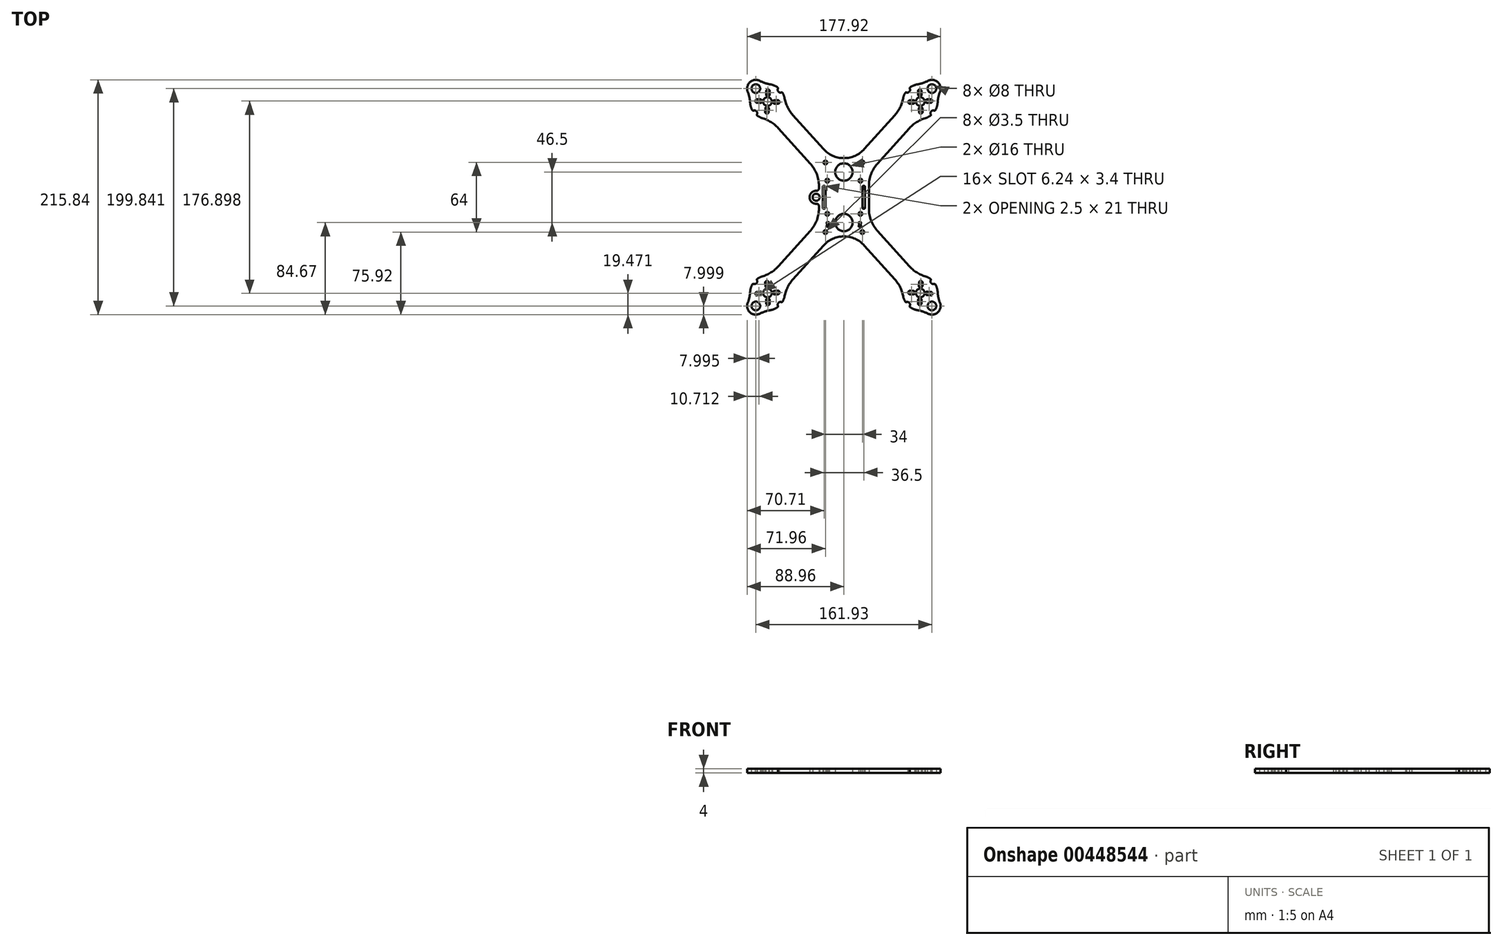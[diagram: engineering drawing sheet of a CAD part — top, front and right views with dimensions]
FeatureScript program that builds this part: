
annotation { "Feature Type Name" : "Feature", "Feature Type Description" : "" }
export const myFeature = defineFeature(function(context is Context, id is Id, definition is map)
    precondition{}
    {
        {
            var Q0;
            Q0=qCreatedBy(makeId("Top.planeOp"),FACE);
            var sketch = newSketch(context, id + "F0", { "sketchPlane" : qUnion([Q0])});
            skLineSegment(sketch, "E0", {"start": v(0, 10) * mm, "end": v(-70.26, 88.03) * mm, "construction": true});
            skCircle(sketch, "E1", {"center": v(-17, 32) * mm, "radius": 1.75 * mm});
            skCircle(sketch, "E2", {"center": v(-15.25, 15.25) * mm, "radius": 1.75 * mm});
            skLineSegment(sketch, "E3", {"start": v(-60.25, 63.46) * mm, "end": v(-30.82, 30.78) * mm});
            skLineSegment(sketch, "E4", {"start": v(-46.87, 75.5) * mm, "end": v(-18.86, 44.4) * mm});
            skLineSegment(sketch, "E5", {"start": v(-18.5, 10.5) * mm, "end": v(-18, 10.5) * mm});
            skArc(sketch, "E6", {"start": v(-54.54, 91) * mm, "mid": v(-55.24, 93.53) * mm, "end": v(-56.34, 95.93) * mm});
            skLineSegment(sketch, "E7.trimOffspring", {"start": v(-68.1, 72.18) * mm, "end": v(-68.1, 72.18) * mm});
            skCircle(sketch, "E8", {"center": v(-70.26, 88.03) * mm, "radius": 14 * mm, "construction": true});
            skCircle(sketch, "E9", {"center": v(-70.26, 88.03) * mm, "radius": 4 * mm});
            skArc(sketch, "E10", {"start": v(-30.5, 30.41) * mm, "mid": v(-30.66, 30.6) * mm, "end": v(-30.82, 30.78) * mm});
            skArc(sketch, "E11", {"start": v(-18.86, 44.4) * mm, "mid": v(-10.32, 38.2) * mm, "end": v(0, 36) * mm});
            skArc(sketch, "E12", {"start": v(0, 31.25) * mm, "mid": v(-8, 23.25) * mm, "end": v(0, 15.25) * mm});
            skPoint(sketch, "E13.visualSharp", {"position": v(-20.22, 10.5) * mm});
            skPoint(sketch, "E14.visualSharp", {"position": v(-54.72, 84.22) * mm});
            skArc(sketch, "E14.filletArc", {"start": v(-54.54, 91) * mm, "mid": v(-51.77, 82.72) * mm, "end": v(-46.87, 75.5) * mm});
            skPoint(sketch, "E15.visualSharp", {"position": v(-68.1, 72.18) * mm});
            skArc(sketch, "E15.filletArc", {"start": v(-60.25, 63.46) * mm, "mid": v(-66.91, 69.09) * mm, "end": v(-74.85, 72.7) * mm});
            skArc(sketch, "E16", {"start": v(-60.63, 99.8) * mm, "mid": v(-60.23, 97.06) * mm, "end": v(-57.54, 96.38) * mm});
            skArc(sketch, "E17", {"start": v(-79.89, 76.26) * mm, "mid": v(-80.3, 79) * mm, "end": v(-82.97, 79.68) * mm});
            skLineSegment(sketch, "E18", {"start": v(-70.26, 88.03) * mm, "end": v(-80.96, 99.92) * mm, "construction": true});
            skLineSegment(sketch, "E19", {"start": v(-70.26, 88.03) * mm, "end": v(-58.37, 98.74) * mm, "construction": true});
            skLineSegment(sketch, "E20", {"start": v(-70.26, 88.03) * mm, "end": v(-82.15, 77.32) * mm, "construction": true});
            skArc(sketch, "E21.trimOffspring", {"start": v(-60.95, 101.04) * mm, "mid": v(-64.15, 102.82) * mm, "end": v(-67.67, 103.82) * mm});
            skArc(sketch, "E22.trimOffspring", {"start": v(-86.23, 87.1) * mm, "mid": v(-85.6, 83.5) * mm, "end": v(-84.17, 80.13) * mm});
            skArc(sketch, "E23.trimOffspring", {"start": v(-79.57, 75.02) * mm, "mid": v(-77.3, 73.66) * mm, "end": v(-74.85, 72.7) * mm});
            skPoint(sketch, "E24.visualSharp", {"position": v(-83.67, 79.3) * mm});
            skArc(sketch, "E24.filletArc", {"start": v(-84.17, 80.13) * mm, "mid": v(-83.66, 79.7) * mm, "end": v(-82.97, 79.68) * mm});
            skPoint(sketch, "E25.visualSharp", {"position": v(-80.34, 75.6) * mm});
            skArc(sketch, "E25.filletArc", {"start": v(-79.89, 76.26) * mm, "mid": v(-79.95, 75.58) * mm, "end": v(-79.57, 75.02) * mm});
            skPoint(sketch, "E26.visualSharp", {"position": v(-60.18, 100.46) * mm});
            skArc(sketch, "E26.filletArc", {"start": v(-60.63, 99.8) * mm, "mid": v(-60.57, 100.48) * mm, "end": v(-60.95, 101.04) * mm});
            skPoint(sketch, "E27.visualSharp", {"position": v(-56.85, 96.75) * mm});
            skArc(sketch, "E27.filletArc", {"start": v(-56.34, 95.93) * mm, "mid": v(-56.86, 96.37) * mm, "end": v(-57.54, 96.38) * mm});
            skArc(sketch, "E28", {"start": v(-77.27, 107.02) * mm, "mid": v(-86.32, 105.87) * mm, "end": v(-88.4, 96.99) * mm});
            skPoint(sketch, "E29.visualSharp", {"position": v(-73.87, 103.62) * mm});
            skArc(sketch, "E29.filletArc", {"start": v(-77.27, 107.02) * mm, "mid": v(-72.6, 105.04) * mm, "end": v(-67.67, 103.82) * mm});
            skPoint(sketch, "E30.visualSharp", {"position": v(-85.38, 93.25) * mm});
            skArc(sketch, "E30.filletArc", {"start": v(-86.23, 87.1) * mm, "mid": v(-86.93, 92.13) * mm, "end": v(-88.4, 96.99) * mm});
            skCircle(sketch, "E31", {"center": v(-80.96, 99.92) * mm, "radius": 4 * mm});
            skLineSegment(sketch, "E32", {"start": v(-17, 9.5) * mm, "end": v(-17, 0) * mm});
            skArc(sketch, "E33.MirrorCS", {"start": v(-60.63, -99.8) * mm, "mid": v(-60.57, -100.48) * mm, "end": v(-60.95, -101.04) * mm});
            skArc(sketch, "E34.MirrorCS", {"start": v(-79.89, -76.26) * mm, "mid": v(-79.95, -75.58) * mm, "end": v(-79.57, -75.02) * mm});
            skArc(sketch, "E35.MirrorCS", {"start": v(-56.34, -95.93) * mm, "mid": v(-56.86, -96.37) * mm, "end": v(-57.54, -96.38) * mm});
            skArc(sketch, "E36.MirrorCS", {"start": v(-60.63, -99.8) * mm, "mid": v(-60.23, -97.06) * mm, "end": v(-57.54, -96.38) * mm});
            skArc(sketch, "E37.MirrorCS", {"start": v(-60.95, -101.04) * mm, "mid": v(-64.15, -102.82) * mm, "end": v(-67.67, -103.82) * mm});
            skArc(sketch, "E38.MirrorCS", {"start": v(-79.89, -76.26) * mm, "mid": v(-80.3, -79) * mm, "end": v(-82.97, -79.68) * mm});
            skArc(sketch, "E39.MirrorCS", {"start": v(-84.17, -80.13) * mm, "mid": v(-83.66, -79.7) * mm, "end": v(-82.97, -79.68) * mm});
            skArc(sketch, "E40.MirrorCS", {"start": v(-86.23, -87.1) * mm, "mid": v(-85.6, -83.5) * mm, "end": v(-84.17, -80.13) * mm});
            skArc(sketch, "E41.MirrorCS", {"start": v(-79.57, -75.02) * mm, "mid": v(-77.3, -73.66) * mm, "end": v(-74.85, -72.7) * mm});
            skArc(sketch, "E42.MirrorCS", {"start": v(-54.54, -91) * mm, "mid": v(-55.24, -93.53) * mm, "end": v(-56.34, -95.93) * mm});
            skLineSegment(sketch, "E43.MirrorCS", {"start": v(-70.26, -88.03) * mm, "end": v(-58.37, -98.74) * mm, "construction": true});
            skArc(sketch, "E44.MirrorCS", {"start": v(-60.25, -63.46) * mm, "mid": v(-66.91, -69.09) * mm, "end": v(-74.85, -72.7) * mm});
            skArc(sketch, "E45.MirrorCS", {"start": v(-54.54, -91) * mm, "mid": v(-51.77, -82.72) * mm, "end": v(-46.87, -75.5) * mm});
            skArc(sketch, "E46.MirrorCS", {"start": v(-77.27, -107.02) * mm, "mid": v(-72.6, -105.04) * mm, "end": v(-67.67, -103.82) * mm});
            skArc(sketch, "E47.MirrorCS", {"start": v(-86.23, -87.1) * mm, "mid": v(-86.93, -92.13) * mm, "end": v(-88.4, -96.99) * mm});
            skCircle(sketch, "E48.MirrorC", {"center": v(-70.26, -88.03) * mm, "radius": 4 * mm});
            skLineSegment(sketch, "E49.MirrorCS", {"start": v(-70.26, -88.03) * mm, "end": v(-82.15, -77.32) * mm, "construction": true});
            skPoint(sketch, "E50.MirrorP", {"position": v(-80.34, -75.6) * mm});
            skPoint(sketch, "E51.MirrorP", {"position": v(-68.1, -72.18) * mm});
            skLineSegment(sketch, "E52.MirrorCS", {"start": v(-68.1, -72.18) * mm, "end": v(-68.1, -72.18) * mm});
            skCircle(sketch, "E53.MirrorC", {"center": v(-80.96, -99.92) * mm, "radius": 4 * mm});
            skPoint(sketch, "E54.MirrorP", {"position": v(-54.72, -84.22) * mm});
            skArc(sketch, "E55.MirrorCS", {"start": v(-77.27, -107.02) * mm, "mid": v(-86.32, -105.87) * mm, "end": v(-88.4, -96.99) * mm});
            skPoint(sketch, "E56.MirrorP", {"position": v(-85.38, -93.25) * mm});
            skPoint(sketch, "E57.MirrorP", {"position": v(-56.85, -96.75) * mm});
            skLineSegment(sketch, "E58.MirrorCS", {"start": v(-70.26, -88.03) * mm, "end": v(-80.96, -99.92) * mm, "construction": true});
            skPoint(sketch, "E59.MirrorP", {"position": v(-60.18, -100.46) * mm});
            skCircle(sketch, "E60.MirrorC", {"center": v(-70.26, -88.03) * mm, "radius": 14 * mm, "construction": true});
            skPoint(sketch, "E61.MirrorP", {"position": v(-83.67, -79.3) * mm});
            skPoint(sketch, "E62.MirrorP", {"position": v(-73.87, -103.62) * mm});
            skLineSegment(sketch, "E63.MirrorCS", {"start": v(-46.87, -75.5) * mm, "end": v(-18.86, -44.4) * mm});
            skLineSegment(sketch, "E64.MirrorCS", {"start": v(-60.25, -63.46) * mm, "end": v(-30.82, -30.78) * mm});
            skArc(sketch, "E65.MirrorCS", {"start": v(-30.5, -30.41) * mm, "mid": v(-30.66, -30.6) * mm, "end": v(-30.82, -30.78) * mm});
            skLineSegment(sketch, "E66.MirrorCS", {"start": v(-17, -9.5) * mm, "end": v(-17, 0) * mm});
            skLineSegment(sketch, "E67.MirrorCS", {"start": v(-18.5, -10.5) * mm, "end": v(-18, -10.5) * mm});
            skPoint(sketch, "E68.MirrorP", {"position": v(-20.22, -10.5) * mm});
            skCircle(sketch, "E69.MirrorC", {"center": v(-17, -32) * mm, "radius": 1.75 * mm});
            skCircle(sketch, "E70.MirrorC", {"center": v(-15.25, -15.25) * mm, "radius": 1.75 * mm});
            skArc(sketch, "E71.MirrorCS", {"start": v(0, -31.25) * mm, "mid": v(-8, -23.25) * mm, "end": v(0, -15.25) * mm});
            skArc(sketch, "E72.MirrorCS", {"start": v(-18.86, -44.4) * mm, "mid": v(-10.32, -38.2) * mm, "end": v(0, -36) * mm});
            skArc(sketch, "E73.MirrorCS", {"start": v(60.63, -99.8) * mm, "mid": v(60.57, -100.48) * mm, "end": v(60.95, -101.04) * mm});
            skArc(sketch, "E74.MirrorCS", {"start": v(79.89, -76.26) * mm, "mid": v(79.95, -75.58) * mm, "end": v(79.57, -75.02) * mm});
            skLineSegment(sketch, "E75.MirrorCS", {"start": v(18.5, 10.5) * mm, "end": v(18, 10.5) * mm});
            skArc(sketch, "E76.MirrorCS", {"start": v(84.17, 80.13) * mm, "mid": v(83.66, 79.7) * mm, "end": v(82.97, 79.68) * mm});
            skArc(sketch, "E77.MirrorCS", {"start": v(79.89, 76.26) * mm, "mid": v(80.3, 79) * mm, "end": v(82.97, 79.68) * mm});
            skArc(sketch, "E78.MirrorCS", {"start": v(84.17, -80.13) * mm, "mid": v(83.66, -79.7) * mm, "end": v(82.97, -79.68) * mm});
            skArc(sketch, "E79.MirrorCS", {"start": v(56.34, -95.93) * mm, "mid": v(56.86, -96.37) * mm, "end": v(57.54, -96.38) * mm});
            skArc(sketch, "E80.MirrorCS", {"start": v(79.89, 76.26) * mm, "mid": v(79.95, 75.58) * mm, "end": v(79.57, 75.02) * mm});
            skArc(sketch, "E81.MirrorCS", {"start": v(56.34, 95.93) * mm, "mid": v(56.86, 96.37) * mm, "end": v(57.54, 96.38) * mm});
            skArc(sketch, "E82.MirrorCS", {"start": v(79.89, -76.26) * mm, "mid": v(80.3, -79) * mm, "end": v(82.97, -79.68) * mm});
            skArc(sketch, "E83.MirrorCS", {"start": v(60.63, -99.8) * mm, "mid": v(60.23, -97.06) * mm, "end": v(57.54, -96.38) * mm});
            skArc(sketch, "E84.MirrorCS", {"start": v(60.63, 99.8) * mm, "mid": v(60.23, 97.06) * mm, "end": v(57.54, 96.38) * mm});
            skArc(sketch, "E85.MirrorCS", {"start": v(60.63, 99.8) * mm, "mid": v(60.57, 100.48) * mm, "end": v(60.95, 101.04) * mm});
            skLineSegment(sketch, "E86.MirrorCS", {"start": v(18.5, -10.5) * mm, "end": v(18, -10.5) * mm});
            skArc(sketch, "E87.MirrorCS", {"start": v(86.23, 87.1) * mm, "mid": v(85.6, 83.5) * mm, "end": v(84.17, 80.13) * mm});
            skArc(sketch, "E88.MirrorCS", {"start": v(54.54, 91) * mm, "mid": v(55.24, 93.53) * mm, "end": v(56.34, 95.93) * mm});
            skArc(sketch, "E89.MirrorCS", {"start": v(79.57, 75.02) * mm, "mid": v(77.3, 73.66) * mm, "end": v(74.85, 72.7) * mm});
            skArc(sketch, "E90.MirrorCS", {"start": v(79.57, -75.02) * mm, "mid": v(77.3, -73.66) * mm, "end": v(74.85, -72.7) * mm});
            skArc(sketch, "E91.MirrorCS", {"start": v(60.95, 101.04) * mm, "mid": v(64.15, 102.82) * mm, "end": v(67.67, 103.82) * mm});
            skArc(sketch, "E92.MirrorCS", {"start": v(77.27, -107.02) * mm, "mid": v(72.6, -105.04) * mm, "end": v(67.67, -103.82) * mm});
            skArc(sketch, "E93.MirrorCS", {"start": v(60.95, -101.04) * mm, "mid": v(64.15, -102.82) * mm, "end": v(67.67, -103.82) * mm});
            skArc(sketch, "E94.MirrorCS", {"start": v(77.27, 107.02) * mm, "mid": v(72.6, 105.04) * mm, "end": v(67.67, 103.82) * mm});
            skArc(sketch, "E95.MirrorCS", {"start": v(54.54, -91) * mm, "mid": v(55.24, -93.53) * mm, "end": v(56.34, -95.93) * mm});
            skArc(sketch, "E96.MirrorCS", {"start": v(86.23, -87.1) * mm, "mid": v(85.6, -83.5) * mm, "end": v(84.17, -80.13) * mm});
            skCircle(sketch, "E97.MirrorC", {"center": v(70.26, -88.03) * mm, "radius": 4 * mm});
            skLineSegment(sketch, "E98.MirrorCS", {"start": v(17, 9.5) * mm, "end": v(17, 0) * mm});
            skCircle(sketch, "E99.MirrorC", {"center": v(17, -32) * mm, "radius": 1.75 * mm});
            skArc(sketch, "E100.MirrorCS", {"start": v(86.23, 87.1) * mm, "mid": v(86.93, 92.13) * mm, "end": v(88.4, 96.99) * mm});
            skCircle(sketch, "E101.MirrorC", {"center": v(17, 32) * mm, "radius": 1.75 * mm});
            skArc(sketch, "E102.MirrorCS", {"start": v(54.54, -91) * mm, "mid": v(51.77, -82.72) * mm, "end": v(46.87, -75.5) * mm});
            skCircle(sketch, "E103.MirrorC", {"center": v(15.25, -15.25) * mm, "radius": 1.75 * mm});
            skCircle(sketch, "E104.MirrorC", {"center": v(15.25, 15.25) * mm, "radius": 1.75 * mm});
            skLineSegment(sketch, "E105.MirrorCS", {"start": v(70.26, 88.03) * mm, "end": v(58.37, 98.74) * mm, "construction": true});
            skLineSegment(sketch, "E106.MirrorCS", {"start": v(70.26, 88.03) * mm, "end": v(82.15, 77.32) * mm, "construction": true});
            skLineSegment(sketch, "E107.MirrorCS", {"start": v(17, -9.5) * mm, "end": v(17, 0) * mm});
            skArc(sketch, "E108.MirrorCS", {"start": v(86.23, -87.1) * mm, "mid": v(86.93, -92.13) * mm, "end": v(88.4, -96.99) * mm});
            skArc(sketch, "E109.MirrorCS", {"start": v(54.54, 91) * mm, "mid": v(51.77, 82.72) * mm, "end": v(46.87, 75.5) * mm});
            skCircle(sketch, "E110.MirrorC", {"center": v(70.26, 88.03) * mm, "radius": 4 * mm});
            skLineSegment(sketch, "E111.MirrorCS", {"start": v(70.26, -88.03) * mm, "end": v(82.15, -77.32) * mm, "construction": true});
            skLineSegment(sketch, "E112.MirrorCS", {"start": v(60.25, -63.46) * mm, "end": v(30.82, -30.78) * mm});
            skPoint(sketch, "E113.MirrorP", {"position": v(54.72, -84.22) * mm});
            skLineSegment(sketch, "E114.MirrorCS", {"start": v(68.1, -72.18) * mm, "end": v(68.1, -72.18) * mm});
            skPoint(sketch, "E115.MirrorP", {"position": v(73.87, -103.62) * mm});
            skLineSegment(sketch, "E116.MirrorCS", {"start": v(70.26, 88.03) * mm, "end": v(80.96, 99.92) * mm, "construction": true});
            skPoint(sketch, "E117.MirrorP", {"position": v(56.85, 96.75) * mm});
            skPoint(sketch, "E118.MirrorP", {"position": v(60.18, 100.46) * mm});
            skPoint(sketch, "E119.MirrorP", {"position": v(85.38, 93.25) * mm});
            skArc(sketch, "E120.MirrorCS", {"start": v(77.27, -107.02) * mm, "mid": v(86.32, -105.87) * mm, "end": v(88.4, -96.99) * mm});
            skArc(sketch, "E121.MirrorCS", {"start": v(60.25, -63.46) * mm, "mid": v(66.91, -69.09) * mm, "end": v(74.85, -72.7) * mm});
            skArc(sketch, "E122.MirrorCS", {"start": v(77.27, 107.02) * mm, "mid": v(86.32, 105.87) * mm, "end": v(88.4, 96.99) * mm});
            skPoint(sketch, "E123.MirrorP", {"position": v(85.38, -93.25) * mm});
            skCircle(sketch, "E124.MirrorC", {"center": v(70.26, -88.03) * mm, "radius": 14 * mm, "construction": true});
            skPoint(sketch, "E125.MirrorP", {"position": v(68.1, 72.18) * mm});
            skPoint(sketch, "E126.MirrorP", {"position": v(56.85, -96.75) * mm});
            skLineSegment(sketch, "E127.MirrorCS", {"start": v(46.87, -75.5) * mm, "end": v(18.86, -44.4) * mm});
            skPoint(sketch, "E128.MirrorP", {"position": v(54.72, 84.22) * mm});
            skPoint(sketch, "E129.MirrorP", {"position": v(80.34, -75.6) * mm});
            skPoint(sketch, "E130.MirrorP", {"position": v(83.67, -79.3) * mm});
            skArc(sketch, "E131.MirrorCS", {"start": v(60.25, 63.46) * mm, "mid": v(66.91, 69.09) * mm, "end": v(74.85, 72.7) * mm});
            skCircle(sketch, "E132.MirrorC", {"center": v(80.96, -99.92) * mm, "radius": 4 * mm});
            skPoint(sketch, "E133.MirrorP", {"position": v(20.22, -10.5) * mm});
            skLineSegment(sketch, "E134.MirrorCS", {"start": v(68.1, 72.18) * mm, "end": v(68.1, 72.18) * mm});
            skLineSegment(sketch, "E135.MirrorCS", {"start": v(70.26, -88.03) * mm, "end": v(58.37, -98.74) * mm, "construction": true});
            skLineSegment(sketch, "E136.MirrorCS", {"start": v(60.25, 63.46) * mm, "end": v(30.82, 30.78) * mm});
            skLineSegment(sketch, "E137.MirrorCS", {"start": v(46.87, 75.5) * mm, "end": v(18.86, 44.4) * mm});
            skPoint(sketch, "E138.MirrorP", {"position": v(83.67, 79.3) * mm});
            skPoint(sketch, "E139.MirrorP", {"position": v(20.22, 10.5) * mm});
            skPoint(sketch, "E140.MirrorP", {"position": v(60.18, -100.46) * mm});
            skPoint(sketch, "E141.MirrorP", {"position": v(68.1, -72.18) * mm});
            skPoint(sketch, "E142.MirrorP", {"position": v(80.34, 75.6) * mm});
            skCircle(sketch, "E143.MirrorC", {"center": v(80.96, 99.92) * mm, "radius": 4 * mm});
            skCircle(sketch, "E144.MirrorC", {"center": v(70.26, 88.03) * mm, "radius": 14 * mm, "construction": true});
            skPoint(sketch, "E145.MirrorP", {"position": v(73.87, 103.62) * mm});
            skArc(sketch, "E146.MirrorCS", {"start": v(30.5, -30.41) * mm, "mid": v(30.66, -30.6) * mm, "end": v(30.82, -30.78) * mm});
            skArc(sketch, "E147.MirrorCS", {"start": v(30.5, 30.41) * mm, "mid": v(30.66, 30.6) * mm, "end": v(30.82, 30.78) * mm});
            skLineSegment(sketch, "E148.MirrorCS", {"start": v(70.26, -88.03) * mm, "end": v(80.96, -99.92) * mm, "construction": true});
            skArc(sketch, "E149.MirrorCS", {"start": v(18.86, 44.4) * mm, "mid": v(10.32, 38.2) * mm, "end": v(0, 36) * mm});
            skArc(sketch, "E150.MirrorCS", {"start": v(18.86, -44.4) * mm, "mid": v(10.32, -38.2) * mm, "end": v(0, -36) * mm});
            skArc(sketch, "E151.MirrorCS", {"start": v(0, -31.25) * mm, "mid": v(8, -23.25) * mm, "end": v(0, -15.25) * mm});
            skArc(sketch, "E152.MirrorCS", {"start": v(0, 31.25) * mm, "mid": v(8, 23.25) * mm, "end": v(0, 15.25) * mm});
            skPoint(sketch, "E153.visualSharp", {"position": v(-17, 10.5) * mm});
            skArc(sketch, "E153.filletArc", {"start": v(-17, 9.5) * mm, "mid": v(-17.3, 10.2) * mm, "end": v(-18, 10.5) * mm});
            skPoint(sketch, "E154.visualSharp", {"position": v(-17, -10.5) * mm});
            skArc(sketch, "E154.filletArc", {"start": v(-18, -10.5) * mm, "mid": v(-17.3, -10.2) * mm, "end": v(-17, -9.5) * mm});
            skPoint(sketch, "E155.visualSharp", {"position": v(17, -10.5) * mm});
            skArc(sketch, "E155.filletArc", {"start": v(17, -9.5) * mm, "mid": v(17.3, -10.2) * mm, "end": v(18, -10.5) * mm});
            skPoint(sketch, "E156.visualSharp", {"position": v(17, 10.5) * mm});
            skArc(sketch, "E156.filletArc", {"start": v(18, 10.5) * mm, "mid": v(17.3, 10.2) * mm, "end": v(17, 9.5) * mm});
            skArc(sketch, "E157", {"start": v(-25.12, 5.99) * mm, "mid": v(-31.5, 0) * mm, "end": v(-25.12, -5.99) * mm});
            skCircle(sketch, "E158", {"center": v(-25.5, 0) * mm, "radius": 3.25 * mm});
            skLineSegment(sketch, "E159", {"start": v(-19.5, 9.5) * mm, "end": v(-19.5, -9.5) * mm});
            skLineSegment(sketch, "E160", {"start": v(-23, 7.98) * mm, "end": v(-23, 10.58) * mm});
            skLineSegment(sketch, "E161.MirrorCS", {"start": v(-23, -7.98) * mm, "end": v(-23, -10.58) * mm});
            skPoint(sketch, "E162.visualSharp", {"position": v(-19.5, -10.5) * mm});
            skArc(sketch, "E162.filletArc", {"start": v(-19.5, -9.5) * mm, "mid": v(-19.2, -10.2) * mm, "end": v(-18.5, -10.5) * mm});
            skPoint(sketch, "E163.visualSharp", {"position": v(-19.5, 10.5) * mm});
            skArc(sketch, "E163.filletArc", {"start": v(-18.5, 10.5) * mm, "mid": v(-19.2, 10.2) * mm, "end": v(-19.5, 9.5) * mm});
            skPoint(sketch, "E164.visualSharp", {"position": v(-23, 18.75) * mm});
            skArc(sketch, "E164.filletArc", {"start": v(-23, 10.58) * mm, "mid": v(-24.94, 21.18) * mm, "end": v(-30.5, 30.41) * mm});
            skPoint(sketch, "E165.visualSharp", {"position": v(-23, -18.75) * mm});
            skArc(sketch, "E165.filletArc", {"start": v(-30.5, -30.41) * mm, "mid": v(-24.94, -21.18) * mm, "end": v(-23, -10.58) * mm});
            skPoint(sketch, "E166.visualSharp", {"position": v(-23, 5.45) * mm});
            skArc(sketch, "E166.filletArc", {"start": v(-25.12, 5.99) * mm, "mid": v(-23.63, 6.53) * mm, "end": v(-23, 7.98) * mm});
            skPoint(sketch, "E167.visualSharp", {"position": v(-23, -5.45) * mm});
            skArc(sketch, "E167.filletArc", {"start": v(-23, -7.98) * mm, "mid": v(-23.63, -6.53) * mm, "end": v(-25.12, -5.99) * mm});
            skArc(sketch, "E168.MirrorCS", {"start": v(23, 10.58) * mm, "mid": v(24.94, 21.18) * mm, "end": v(30.5, 30.41) * mm});
            skArc(sketch, "E169.MirrorCS", {"start": v(30.5, -30.41) * mm, "mid": v(24.94, -21.18) * mm, "end": v(23, -10.58) * mm});
            skLineSegment(sketch, "E170", {"start": v(23, 10.58) * mm, "end": v(23, -10.58) * mm});
            skLineSegment(sketch, "E171.MirrorCS", {"start": v(19.5, 9.5) * mm, "end": v(19.5, -9.5) * mm});
            skArc(sketch, "E172.MirrorCS", {"start": v(18.5, 10.5) * mm, "mid": v(19.2, 10.2) * mm, "end": v(19.5, 9.5) * mm});
            skArc(sketch, "E173.MirrorCS", {"start": v(19.5, -9.5) * mm, "mid": v(19.2, -10.2) * mm, "end": v(18.5, -10.5) * mm});
            skSolve(sketch);
        }
        {
            var Q0;
            Q0=makeQuery(id+"F0.imprint","IMPRINT",FACE,{"disambiguationData":[TD([[makeQuery(id+"F0.imprint","IMPRINT",EDGE,{"derivedFrom":sQuery(id+"F0.wireOp",EDGE,"E1")}),-1.0]])]});
            extrude(context, id + "F1", {"entities" : qUnion([Q0]), "depth" : 4 * mm});
        }
        {
            var Q0;
            Q0=makeQuery(id+"F1.opExtrude","CAP_FACE",FACE,{"disambiguationData":[OSD([sQuery(id+"F0.wireOp",EDGE,"E1"),sQuery(id+"F0.wireOp",EDGE,"E2"),sQuery(id+"F0.wireOp",EDGE,"E3"),sQuery(id+"F0.wireOp",EDGE,"E4"),sQuery(id+"F0.wireOp",EDGE,"E5"),sQuery(id+"F0.wireOp",EDGE,"E6"),sQuery(id+"F0.wireOp",EDGE,"E9"),sQuery(id+"F0.wireOp",EDGE,"caexf3GR-ABRh-FGbM-1E2W-Yq8lZNTBThtG"),sQuery(id+"F0.wireOp",EDGE,"E10"),sQuery(id+"F0.wireOp",EDGE,"E11"),sQuery(id+"F0.wireOp",EDGE,"lrYDMexf-cjIa-o1B8-912M-ilXSL09QYGVs"),sQuery(id+"F0.wireOp",EDGE,"E12"),sQuery(id+"F0.wireOp",EDGE,"69b210a8-4be9-466b-96a2-185d49c69fcb.trimOffspring"),sQuery(id+"F0.wireOp",EDGE,"E13.filletArc"),sQuery(id+"F0.wireOp",EDGE,"E14.filletArc"),sQuery(id+"F0.wireOp",EDGE,"E15.filletArc"),sQuery(id+"F0.wireOp",EDGE,"XlwXw7Ia-4k9A-3DB6-GY0S-PxJLlph5xH7B"),sQuery(id+"F0.wireOp",EDGE,"E16"),sQuery(id+"F0.wireOp",EDGE,"E17"),sQuery(id+"F0.wireOp",EDGE,"E21.trimOffspring"),sQuery(id+"F0.wireOp",EDGE,"E22.trimOffspring"),sQuery(id+"F0.wireOp",EDGE,"E23.trimOffspring"),sQuery(id+"F0.wireOp",EDGE,"465da84a-1fcb-458c-8af7-43b6bd39abb9.filletArc"),sQuery(id+"F0.wireOp",EDGE,"546c875d-b3e8-496f-961f-fee2dbec4bf7.filletArc"),sQuery(id+"F0.wireOp",EDGE,"E24.filletArc"),sQuery(id+"F0.wireOp",EDGE,"E25.filletArc"),sQuery(id+"F0.wireOp",EDGE,"E26.filletArc"),sQuery(id+"F0.wireOp",EDGE,"E27.filletArc")])],"isStart":false});
            var sketch = newSketch(context, id + "F2", { "sketchPlane" : qUnion([Q0])});
            skLineSegment(sketch, "E174", {"start": v(-70.26, 88.03) * mm, "end": v(-18.5, 30.55) * mm, "construction": true});
            skLineSegment(sketch, "E175", {"start": v(-70.26, 88.03) * mm, "end": v(-63.77, 87.7) * mm, "construction": true});
            skLineSegment(sketch, "E176", {"start": v(-63.77, 87.7) * mm, "end": v(-60.77, 87.53) * mm, "construction": true});
            skArc(sketch, "E177.0.startCap", {"start": v(-63.85, 86.07) * mm, "mid": v(-65.4, 87.78) * mm, "end": v(-63.68, 89.31) * mm});
            skArc(sketch, "E177.0.endCap", {"start": v(-60.69, 89.16) * mm, "mid": v(-59.15, 87.45) * mm, "end": v(-60.86, 85.91) * mm});
            skLineSegment(sketch, "E177.0.left", {"start": v(-63.68, 89.31) * mm, "end": v(-60.69, 89.16) * mm});
            skLineSegment(sketch, "E177.0.right", {"start": v(-63.85, 86.07) * mm, "end": v(-60.86, 85.91) * mm});
            skLineSegment(sketch, "E178.1.0", {"start": v(-71.54, 94.6) * mm, "end": v(-71.38, 97.6) * mm});
            skArc(sketch, "E178.1.1", {"start": v(-68.3, 94.44) * mm, "mid": v(-70, 92.9) * mm, "end": v(-71.54, 94.6) * mm});
            skLineSegment(sketch, "E178.1.2", {"start": v(-68.3, 94.44) * mm, "end": v(-68.14, 97.43) * mm});
            skArc(sketch, "E178.1.3", {"start": v(-71.38, 97.6) * mm, "mid": v(-69.68, 99.14) * mm, "end": v(-68.14, 97.43) * mm});
            skLineSegment(sketch, "E178.2.0", {"start": v(-76.83, 86.75) * mm, "end": v(-79.83, 86.9) * mm});
            skArc(sketch, "E178.2.1", {"start": v(-76.66, 90) * mm, "mid": v(-75.13, 88.29) * mm, "end": v(-76.83, 86.75) * mm});
            skLineSegment(sketch, "E178.2.2", {"start": v(-76.66, 90) * mm, "end": v(-79.66, 90.15) * mm});
            skArc(sketch, "E178.2.3", {"start": v(-79.83, 86.9) * mm, "mid": v(-81.37, 88.61) * mm, "end": v(-79.66, 90.15) * mm});
            skLineSegment(sketch, "E178.3.0", {"start": v(-68.98, 81.45) * mm, "end": v(-69.13, 78.46) * mm});
            skArc(sketch, "E178.3.1", {"start": v(-72.22, 81.62) * mm, "mid": v(-70.51, 83.16) * mm, "end": v(-68.98, 81.45) * mm});
            skLineSegment(sketch, "E178.3.2", {"start": v(-72.22, 81.62) * mm, "end": v(-72.38, 78.63) * mm});
            skArc(sketch, "E178.3.3", {"start": v(-69.13, 78.46) * mm, "mid": v(-70.84, 76.92) * mm, "end": v(-72.38, 78.63) * mm});
            skPoint(sketch, "E178.center", {"position": v(-70.26, 88.03) * mm});
            skArc(sketch, "E179.MirrorCS", {"start": v(63.85, 86.07) * mm, "mid": v(65.4, 87.78) * mm, "end": v(63.68, 89.31) * mm});
            skLineSegment(sketch, "E180.MirrorCS", {"start": v(76.66, 90) * mm, "end": v(79.66, 90.15) * mm});
            skArc(sketch, "E181.MirrorCS", {"start": v(79.83, 86.9) * mm, "mid": v(81.37, 88.61) * mm, "end": v(79.66, 90.15) * mm});
            skLineSegment(sketch, "E182.MirrorCS", {"start": v(63.77, 87.7) * mm, "end": v(60.77, 87.53) * mm, "construction": true});
            skLineSegment(sketch, "E183.MirrorCS", {"start": v(63.68, 89.31) * mm, "end": v(60.69, 89.16) * mm});
            skArc(sketch, "E184.MirrorCS", {"start": v(60.69, 89.16) * mm, "mid": v(59.15, 87.45) * mm, "end": v(60.86, 85.91) * mm});
            skArc(sketch, "E185.MirrorCS", {"start": v(68.3, 94.44) * mm, "mid": v(70, 92.9) * mm, "end": v(71.54, 94.6) * mm});
            skArc(sketch, "E186.MirrorCS", {"start": v(71.38, 97.6) * mm, "mid": v(69.68, 99.14) * mm, "end": v(68.14, 97.43) * mm});
            skLineSegment(sketch, "E187.MirrorCS", {"start": v(68.3, 94.44) * mm, "end": v(68.14, 97.43) * mm});
            skLineSegment(sketch, "E188.MirrorCS", {"start": v(76.83, 86.75) * mm, "end": v(79.83, 86.9) * mm});
            skArc(sketch, "E189.MirrorCS", {"start": v(76.66, 90) * mm, "mid": v(75.13, 88.29) * mm, "end": v(76.83, 86.75) * mm});
            skLineSegment(sketch, "E190.MirrorCS", {"start": v(68.98, 81.45) * mm, "end": v(69.13, 78.46) * mm});
            skArc(sketch, "E191.MirrorCS", {"start": v(69.13, 78.46) * mm, "mid": v(70.84, 76.92) * mm, "end": v(72.38, 78.63) * mm});
            skLineSegment(sketch, "E192.MirrorCS", {"start": v(63.85, 86.07) * mm, "end": v(60.86, 85.91) * mm});
            skLineSegment(sketch, "E193.MirrorCS", {"start": v(71.54, 94.6) * mm, "end": v(71.38, 97.6) * mm});
            skArc(sketch, "E194.MirrorCS", {"start": v(72.22, 81.62) * mm, "mid": v(70.51, 83.16) * mm, "end": v(68.98, 81.45) * mm});
            skLineSegment(sketch, "E195.MirrorCS", {"start": v(72.22, 81.62) * mm, "end": v(72.38, 78.63) * mm});
            skLineSegment(sketch, "E196.MirrorCS", {"start": v(70.26, 88.03) * mm, "end": v(63.77, 87.7) * mm, "construction": true});
            skPoint(sketch, "E197.MirrorP", {"position": v(70.26, 88.03) * mm});
            skArc(sketch, "E198.MirrorCS", {"start": v(-63.85, -86.07) * mm, "mid": v(-65.4, -87.78) * mm, "end": v(-63.68, -89.31) * mm});
            skArc(sketch, "E199.MirrorCS", {"start": v(60.69, -89.16) * mm, "mid": v(59.15, -87.45) * mm, "end": v(60.86, -85.91) * mm});
            skLineSegment(sketch, "E200.MirrorCS", {"start": v(63.85, -86.07) * mm, "end": v(60.86, -85.91) * mm});
            skLineSegment(sketch, "E201.MirrorCS", {"start": v(63.68, -89.31) * mm, "end": v(60.69, -89.16) * mm});
            skLineSegment(sketch, "E202.MirrorCS", {"start": v(-76.66, -90) * mm, "end": v(-79.66, -90.15) * mm});
            skLineSegment(sketch, "E203.MirrorCS", {"start": v(63.77, -87.7) * mm, "end": v(60.77, -87.53) * mm, "construction": true});
            skArc(sketch, "E204.MirrorCS", {"start": v(-76.66, -90) * mm, "mid": v(-75.13, -88.29) * mm, "end": v(-76.83, -86.75) * mm});
            skLineSegment(sketch, "E205.MirrorCS", {"start": v(-63.85, -86.07) * mm, "end": v(-60.86, -85.91) * mm});
            skArc(sketch, "E206.MirrorCS", {"start": v(63.85, -86.07) * mm, "mid": v(65.4, -87.78) * mm, "end": v(63.68, -89.31) * mm});
            skLineSegment(sketch, "E207.MirrorCS", {"start": v(-63.68, -89.31) * mm, "end": v(-60.69, -89.16) * mm});
            skArc(sketch, "E208.MirrorCS", {"start": v(-60.69, -89.16) * mm, "mid": v(-59.15, -87.45) * mm, "end": v(-60.86, -85.91) * mm});
            skLineSegment(sketch, "E209.MirrorCS", {"start": v(-63.77, -87.7) * mm, "end": v(-60.77, -87.53) * mm, "construction": true});
            skArc(sketch, "E210.MirrorCS", {"start": v(76.66, -90) * mm, "mid": v(75.13, -88.29) * mm, "end": v(76.83, -86.75) * mm});
            skLineSegment(sketch, "E211.MirrorCS", {"start": v(71.54, -94.6) * mm, "end": v(71.38, -97.6) * mm});
            skArc(sketch, "E212.MirrorCS", {"start": v(-72.22, -81.62) * mm, "mid": v(-70.51, -83.16) * mm, "end": v(-68.98, -81.45) * mm});
            skLineSegment(sketch, "E213.MirrorCS", {"start": v(68.98, -81.45) * mm, "end": v(69.13, -78.46) * mm});
            skArc(sketch, "E214.MirrorCS", {"start": v(79.83, -86.9) * mm, "mid": v(81.37, -88.61) * mm, "end": v(79.66, -90.15) * mm});
            skLineSegment(sketch, "E215.MirrorCS", {"start": v(68.3, -94.44) * mm, "end": v(68.14, -97.43) * mm});
            skLineSegment(sketch, "E216.MirrorCS", {"start": v(76.66, -90) * mm, "end": v(79.66, -90.15) * mm});
            skLineSegment(sketch, "E217.MirrorCS", {"start": v(-68.98, -81.45) * mm, "end": v(-69.13, -78.46) * mm});
            skArc(sketch, "E218.MirrorCS", {"start": v(69.13, -78.46) * mm, "mid": v(70.84, -76.92) * mm, "end": v(72.38, -78.63) * mm});
            skLineSegment(sketch, "E219.MirrorCS", {"start": v(76.83, -86.75) * mm, "end": v(79.83, -86.9) * mm});
            skLineSegment(sketch, "E220.MirrorCS", {"start": v(-72.22, -81.62) * mm, "end": v(-72.38, -78.63) * mm});
            skArc(sketch, "E221.MirrorCS", {"start": v(71.38, -97.6) * mm, "mid": v(69.68, -99.14) * mm, "end": v(68.14, -97.43) * mm});
            skLineSegment(sketch, "E222.MirrorCS", {"start": v(72.22, -81.62) * mm, "end": v(72.38, -78.63) * mm});
            skArc(sketch, "E223.MirrorCS", {"start": v(-69.13, -78.46) * mm, "mid": v(-70.84, -76.92) * mm, "end": v(-72.38, -78.63) * mm});
            skArc(sketch, "E224.MirrorCS", {"start": v(72.22, -81.62) * mm, "mid": v(70.51, -83.16) * mm, "end": v(68.98, -81.45) * mm});
            skLineSegment(sketch, "E225.MirrorCS", {"start": v(-76.83, -86.75) * mm, "end": v(-79.83, -86.9) * mm});
            skArc(sketch, "E226.MirrorCS", {"start": v(68.3, -94.44) * mm, "mid": v(70, -92.9) * mm, "end": v(71.54, -94.6) * mm});
            skLineSegment(sketch, "E227.MirrorCS", {"start": v(-71.54, -94.6) * mm, "end": v(-71.38, -97.6) * mm});
            skArc(sketch, "E228.MirrorCS", {"start": v(-68.3, -94.44) * mm, "mid": v(-70, -92.9) * mm, "end": v(-71.54, -94.6) * mm});
            skArc(sketch, "E229.MirrorCS", {"start": v(-71.38, -97.6) * mm, "mid": v(-69.68, -99.14) * mm, "end": v(-68.14, -97.43) * mm});
            skArc(sketch, "E230.MirrorCS", {"start": v(-79.83, -86.9) * mm, "mid": v(-81.37, -88.61) * mm, "end": v(-79.66, -90.15) * mm});
            skLineSegment(sketch, "E231.MirrorCS", {"start": v(-68.3, -94.44) * mm, "end": v(-68.14, -97.43) * mm});
            skLineSegment(sketch, "E232.MirrorCS", {"start": v(70.26, -88.03) * mm, "end": v(63.77, -87.7) * mm, "construction": true});
            skLineSegment(sketch, "E233.MirrorCS", {"start": v(-70.26, -88.03) * mm, "end": v(-63.77, -87.7) * mm, "construction": true});
            skPoint(sketch, "E234.MirrorP", {"position": v(-70.26, -88.03) * mm});
            skPoint(sketch, "E235.MirrorP", {"position": v(70.26, -88.03) * mm});
            skSolve(sketch);
        }
        {
            var Q0;
            Q0=qSketchRegion(id+"F2",true);
            extrude(context, id + "F3", {"entities" : qUnion([Q0]), "operationType" : NewBodyOperationType.REMOVE, "oppositeDirection" : true, "depth" : 25 * mm});
        }
        {
            var Q0;
            Q0=makeQuery(id+"F1.opExtrude","CAP_FACE",FACE,{"disambiguationData":[OSD([sQuery(id+"F0.wireOp",EDGE,"E1"),sQuery(id+"F0.wireOp",EDGE,"E2"),sQuery(id+"F0.wireOp",EDGE,"E3"),sQuery(id+"F0.wireOp",EDGE,"E4"),sQuery(id+"F0.wireOp",EDGE,"E5"),sQuery(id+"F0.wireOp",EDGE,"E6"),sQuery(id+"F0.wireOp",EDGE,"E9"),sQuery(id+"F0.wireOp",EDGE,"E10"),sQuery(id+"F0.wireOp",EDGE,"E11"),sQuery(id+"F0.wireOp",EDGE,"E12"),sQuery(id+"F0.wireOp",EDGE,"E14.filletArc"),sQuery(id+"F0.wireOp",EDGE,"E15.filletArc"),sQuery(id+"F0.wireOp",EDGE,"E16"),sQuery(id+"F0.wireOp",EDGE,"E17"),sQuery(id+"F0.wireOp",EDGE,"E21.trimOffspring"),sQuery(id+"F0.wireOp",EDGE,"E22.trimOffspring"),sQuery(id+"F0.wireOp",EDGE,"E23.trimOffspring"),sQuery(id+"F0.wireOp",EDGE,"E24.filletArc"),sQuery(id+"F0.wireOp",EDGE,"E25.filletArc"),sQuery(id+"F0.wireOp",EDGE,"E26.filletArc"),sQuery(id+"F0.wireOp",EDGE,"E27.filletArc"),sQuery(id+"F0.wireOp",EDGE,"E28"),sQuery(id+"F0.wireOp",EDGE,"E29.filletArc"),sQuery(id+"F0.wireOp",EDGE,"E30.filletArc"),sQuery(id+"F0.wireOp",EDGE,"E31"),sQuery(id+"F0.wireOp",EDGE,"E32"),sQuery(id+"F0.wireOp",EDGE,"E33.MirrorCS"),sQuery(id+"F0.wireOp",EDGE,"E34.MirrorCS"),sQuery(id+"F0.wireOp",EDGE,"E35.MirrorCS"),sQuery(id+"F0.wireOp",EDGE,"E36.MirrorCS"),sQuery(id+"F0.wireOp",EDGE,"E37.MirrorCS"),sQuery(id+"F0.wireOp",EDGE,"E38.MirrorCS"),sQuery(id+"F0.wireOp",EDGE,"E39.MirrorCS"),sQuery(id+"F0.wireOp",EDGE,"E40.MirrorCS"),sQuery(id+"F0.wireOp",EDGE,"E41.MirrorCS"),sQuery(id+"F0.wireOp",EDGE,"E42.MirrorCS"),sQuery(id+"F0.wireOp",EDGE,"E44.MirrorCS"),sQuery(id+"F0.wireOp",EDGE,"E45.MirrorCS"),sQuery(id+"F0.wireOp",EDGE,"E46.MirrorCS"),sQuery(id+"F0.wireOp",EDGE,"E47.MirrorCS"),sQuery(id+"F0.wireOp",EDGE,"E48.MirrorC"),sQuery(id+"F0.wireOp",EDGE,"E53.MirrorC"),sQuery(id+"F0.wireOp",EDGE,"E55.MirrorCS"),sQuery(id+"F0.wireOp",EDGE,"E63.MirrorCS"),sQuery(id+"F0.wireOp",EDGE,"E64.MirrorCS"),sQuery(id+"F0.wireOp",EDGE,"E65.MirrorCS"),sQuery(id+"F0.wireOp",EDGE,"E66.MirrorCS"),sQuery(id+"F0.wireOp",EDGE,"E67.MirrorCS"),sQuery(id+"F0.wireOp",EDGE,"E69.MirrorC"),sQuery(id+"F0.wireOp",EDGE,"E70.MirrorC"),sQuery(id+"F0.wireOp",EDGE,"E71.MirrorCS"),sQuery(id+"F0.wireOp",EDGE,"E72.MirrorCS"),sQuery(id+"F0.wireOp",EDGE,"E73.MirrorCS"),sQuery(id+"F0.wireOp",EDGE,"E74.MirrorCS"),sQuery(id+"F0.wireOp",EDGE,"E75.MirrorCS"),sQuery(id+"F0.wireOp",EDGE,"E76.MirrorCS"),sQuery(id+"F0.wireOp",EDGE,"E77.MirrorCS"),sQuery(id+"F0.wireOp",EDGE,"E78.MirrorCS"),sQuery(id+"F0.wireOp",EDGE,"E79.MirrorCS"),sQuery(id+"F0.wireOp",EDGE,"E80.MirrorCS"),sQuery(id+"F0.wireOp",EDGE,"E81.MirrorCS"),sQuery(id+"F0.wireOp",EDGE,"E82.MirrorCS"),sQuery(id+"F0.wireOp",EDGE,"E83.MirrorCS"),sQuery(id+"F0.wireOp",EDGE,"E84.MirrorCS"),sQuery(id+"F0.wireOp",EDGE,"E85.MirrorCS"),sQuery(id+"F0.wireOp",EDGE,"E86.MirrorCS"),sQuery(id+"F0.wireOp",EDGE,"E87.MirrorCS"),sQuery(id+"F0.wireOp",EDGE,"E88.MirrorCS"),sQuery(id+"F0.wireOp",EDGE,"E89.MirrorCS"),sQuery(id+"F0.wireOp",EDGE,"E90.MirrorCS"),sQuery(id+"F0.wireOp",EDGE,"E91.MirrorCS"),sQuery(id+"F0.wireOp",EDGE,"E92.MirrorCS"),sQuery(id+"F0.wireOp",EDGE,"E93.MirrorCS"),sQuery(id+"F0.wireOp",EDGE,"E94.MirrorCS"),sQuery(id+"F0.wireOp",EDGE,"E95.MirrorCS"),sQuery(id+"F0.wireOp",EDGE,"E96.MirrorCS"),sQuery(id+"F0.wireOp",EDGE,"E97.MirrorC"),sQuery(id+"F0.wireOp",EDGE,"E98.MirrorCS"),sQuery(id+"F0.wireOp",EDGE,"E99.MirrorC"),sQuery(id+"F0.wireOp",EDGE,"E100.MirrorCS"),sQuery(id+"F0.wireOp",EDGE,"E101.MirrorC"),sQuery(id+"F0.wireOp",EDGE,"E102.MirrorCS"),sQuery(id+"F0.wireOp",EDGE,"E103.MirrorC"),sQuery(id+"F0.wireOp",EDGE,"E104.MirrorC"),sQuery(id+"F0.wireOp",EDGE,"E107.MirrorCS"),sQuery(id+"F0.wireOp",EDGE,"E108.MirrorCS"),sQuery(id+"F0.wireOp",EDGE,"E109.MirrorCS"),sQuery(id+"F0.wireOp",EDGE,"E110.MirrorC"),sQuery(id+"F0.wireOp",EDGE,"E112.MirrorCS"),sQuery(id+"F0.wireOp",EDGE,"E120.MirrorCS"),sQuery(id+"F0.wireOp",EDGE,"E121.MirrorCS"),sQuery(id+"F0.wireOp",EDGE,"E122.MirrorCS"),sQuery(id+"F0.wireOp",EDGE,"E127.MirrorCS"),sQuery(id+"F0.wireOp",EDGE,"E131.MirrorCS"),sQuery(id+"F0.wireOp",EDGE,"E132.MirrorC"),sQuery(id+"F0.wireOp",EDGE,"E136.MirrorCS"),sQuery(id+"F0.wireOp",EDGE,"E137.MirrorCS"),sQuery(id+"F0.wireOp",EDGE,"E143.MirrorC"),sQuery(id+"F0.wireOp",EDGE,"E146.MirrorCS"),sQuery(id+"F0.wireOp",EDGE,"E147.MirrorCS"),sQuery(id+"F0.wireOp",EDGE,"E149.MirrorCS"),sQuery(id+"F0.wireOp",EDGE,"E150.MirrorCS"),sQuery(id+"F0.wireOp",EDGE,"E151.MirrorCS"),sQuery(id+"F0.wireOp",EDGE,"E152.MirrorCS"),sQuery(id+"F0.wireOp",EDGE,"E153.filletArc"),sQuery(id+"F0.wireOp",EDGE,"E154.filletArc"),sQuery(id+"F0.wireOp",EDGE,"E155.filletArc"),sQuery(id+"F0.wireOp",EDGE,"E156.filletArc"),sQuery(id+"F0.wireOp",EDGE,"E157"),sQuery(id+"F0.wireOp",EDGE,"E158"),sQuery(id+"F0.wireOp",EDGE,"E159"),sQuery(id+"F0.wireOp",EDGE,"E160"),sQuery(id+"F0.wireOp",EDGE,"E161.MirrorCS"),sQuery(id+"F0.wireOp",EDGE,"E162.filletArc"),sQuery(id+"F0.wireOp",EDGE,"E163.filletArc"),sQuery(id+"F0.wireOp",EDGE,"E164.filletArc"),sQuery(id+"F0.wireOp",EDGE,"E165.filletArc"),sQuery(id+"F0.wireOp",EDGE,"E166.filletArc"),sQuery(id+"F0.wireOp",EDGE,"E167.filletArc"),sQuery(id+"F0.wireOp",EDGE,"E168.MirrorCS"),sQuery(id+"F0.wireOp",EDGE,"E169.MirrorCS"),sQuery(id+"F0.wireOp",EDGE,"E170"),sQuery(id+"F0.wireOp",EDGE,"E171.MirrorCS"),sQuery(id+"F0.wireOp",EDGE,"E172.MirrorCS"),sQuery(id+"F0.wireOp",EDGE,"E173.MirrorCS"),sQuery(id+"F0.wireOp",EDGE,"cdnWEf1f-NTT4-Ris5-EAQB-sNyYZjwwmCeJ")])],"isStart":false});
            var sketch = newSketch(context, id + "F4", { "sketchPlane" : qUnion([Q0])});
            skLineSegment(sketch, "E236.bottom", {"start": v(-15.5, -23) * mm, "end": v(-14, -23) * mm});
            skLineSegment(sketch, "E236.top", {"start": v(-15.5, -27) * mm, "end": v(-14, -27) * mm});
            skLineSegment(sketch, "E236.left", {"start": v(-15.5, -23) * mm, "end": v(-15.5, -27) * mm});
            skLineSegment(sketch, "E236.right", {"start": v(-14, -23) * mm, "end": v(-14, -27) * mm});
            skLineSegment(sketch, "E237.MirrorCS", {"start": v(15.5, -23) * mm, "end": v(15.5, -27) * mm});
            skLineSegment(sketch, "E238.MirrorCS", {"start": v(15.5, -27) * mm, "end": v(14, -27) * mm});
            skLineSegment(sketch, "E239.MirrorCS", {"start": v(14, -23) * mm, "end": v(14, -27) * mm});
            skLineSegment(sketch, "E240.MirrorCS", {"start": v(15.5, -23) * mm, "end": v(14, -23) * mm});
            skSolve(sketch);
        }
        {
            var Q0;
            Q0 = qSketchRegion(id + "F4", true);
            extrude(context, id + "F5", {"entities" : qUnion([Q0]), "operationType" : NewBodyOperationType.REMOVE, "oppositeDirection" : true, "depth" : 25 * mm});
        }
        {
            var Q0;
            Q0=makeQuery(id+"F1.opExtrude","CAP_FACE",FACE,{"disambiguationData":[OSD([sQuery(id+"F0.wireOp",EDGE,"E1"),sQuery(id+"F0.wireOp",EDGE,"E2"),sQuery(id+"F0.wireOp",EDGE,"E3"),sQuery(id+"F0.wireOp",EDGE,"E4"),sQuery(id+"F0.wireOp",EDGE,"E5"),sQuery(id+"F0.wireOp",EDGE,"E6"),sQuery(id+"F0.wireOp",EDGE,"E9"),sQuery(id+"F0.wireOp",EDGE,"E10"),sQuery(id+"F0.wireOp",EDGE,"E11"),sQuery(id+"F0.wireOp",EDGE,"E12"),sQuery(id+"F0.wireOp",EDGE,"E14.filletArc"),sQuery(id+"F0.wireOp",EDGE,"E15.filletArc"),sQuery(id+"F0.wireOp",EDGE,"E16"),sQuery(id+"F0.wireOp",EDGE,"E17"),sQuery(id+"F0.wireOp",EDGE,"E21.trimOffspring"),sQuery(id+"F0.wireOp",EDGE,"E22.trimOffspring"),sQuery(id+"F0.wireOp",EDGE,"E23.trimOffspring"),sQuery(id+"F0.wireOp",EDGE,"E24.filletArc"),sQuery(id+"F0.wireOp",EDGE,"E25.filletArc"),sQuery(id+"F0.wireOp",EDGE,"E26.filletArc"),sQuery(id+"F0.wireOp",EDGE,"E27.filletArc"),sQuery(id+"F0.wireOp",EDGE,"E28"),sQuery(id+"F0.wireOp",EDGE,"E29.filletArc"),sQuery(id+"F0.wireOp",EDGE,"E30.filletArc"),sQuery(id+"F0.wireOp",EDGE,"E31"),sQuery(id+"F0.wireOp",EDGE,"E32"),sQuery(id+"F0.wireOp",EDGE,"E33.MirrorCS"),sQuery(id+"F0.wireOp",EDGE,"E34.MirrorCS"),sQuery(id+"F0.wireOp",EDGE,"E35.MirrorCS"),sQuery(id+"F0.wireOp",EDGE,"E36.MirrorCS"),sQuery(id+"F0.wireOp",EDGE,"E37.MirrorCS"),sQuery(id+"F0.wireOp",EDGE,"E38.MirrorCS"),sQuery(id+"F0.wireOp",EDGE,"E39.MirrorCS"),sQuery(id+"F0.wireOp",EDGE,"E40.MirrorCS"),sQuery(id+"F0.wireOp",EDGE,"E41.MirrorCS"),sQuery(id+"F0.wireOp",EDGE,"E42.MirrorCS"),sQuery(id+"F0.wireOp",EDGE,"E44.MirrorCS"),sQuery(id+"F0.wireOp",EDGE,"E45.MirrorCS"),sQuery(id+"F0.wireOp",EDGE,"E46.MirrorCS"),sQuery(id+"F0.wireOp",EDGE,"E47.MirrorCS"),sQuery(id+"F0.wireOp",EDGE,"E48.MirrorC"),sQuery(id+"F0.wireOp",EDGE,"E53.MirrorC"),sQuery(id+"F0.wireOp",EDGE,"E55.MirrorCS"),sQuery(id+"F0.wireOp",EDGE,"E63.MirrorCS"),sQuery(id+"F0.wireOp",EDGE,"E64.MirrorCS"),sQuery(id+"F0.wireOp",EDGE,"E65.MirrorCS"),sQuery(id+"F0.wireOp",EDGE,"E66.MirrorCS"),sQuery(id+"F0.wireOp",EDGE,"E67.MirrorCS"),sQuery(id+"F0.wireOp",EDGE,"E69.MirrorC"),sQuery(id+"F0.wireOp",EDGE,"E70.MirrorC"),sQuery(id+"F0.wireOp",EDGE,"E71.MirrorCS"),sQuery(id+"F0.wireOp",EDGE,"E72.MirrorCS"),sQuery(id+"F0.wireOp",EDGE,"E73.MirrorCS"),sQuery(id+"F0.wireOp",EDGE,"E74.MirrorCS"),sQuery(id+"F0.wireOp",EDGE,"E75.MirrorCS"),sQuery(id+"F0.wireOp",EDGE,"E76.MirrorCS"),sQuery(id+"F0.wireOp",EDGE,"E77.MirrorCS"),sQuery(id+"F0.wireOp",EDGE,"E78.MirrorCS"),sQuery(id+"F0.wireOp",EDGE,"E79.MirrorCS"),sQuery(id+"F0.wireOp",EDGE,"E80.MirrorCS"),sQuery(id+"F0.wireOp",EDGE,"E81.MirrorCS"),sQuery(id+"F0.wireOp",EDGE,"E82.MirrorCS"),sQuery(id+"F0.wireOp",EDGE,"E83.MirrorCS"),sQuery(id+"F0.wireOp",EDGE,"E84.MirrorCS"),sQuery(id+"F0.wireOp",EDGE,"E85.MirrorCS"),sQuery(id+"F0.wireOp",EDGE,"E86.MirrorCS"),sQuery(id+"F0.wireOp",EDGE,"E87.MirrorCS"),sQuery(id+"F0.wireOp",EDGE,"E88.MirrorCS"),sQuery(id+"F0.wireOp",EDGE,"E89.MirrorCS"),sQuery(id+"F0.wireOp",EDGE,"E90.MirrorCS"),sQuery(id+"F0.wireOp",EDGE,"E91.MirrorCS"),sQuery(id+"F0.wireOp",EDGE,"E92.MirrorCS"),sQuery(id+"F0.wireOp",EDGE,"E93.MirrorCS"),sQuery(id+"F0.wireOp",EDGE,"E94.MirrorCS"),sQuery(id+"F0.wireOp",EDGE,"E95.MirrorCS"),sQuery(id+"F0.wireOp",EDGE,"E96.MirrorCS"),sQuery(id+"F0.wireOp",EDGE,"E97.MirrorC"),sQuery(id+"F0.wireOp",EDGE,"E98.MirrorCS"),sQuery(id+"F0.wireOp",EDGE,"E99.MirrorC"),sQuery(id+"F0.wireOp",EDGE,"E100.MirrorCS"),sQuery(id+"F0.wireOp",EDGE,"E101.MirrorC"),sQuery(id+"F0.wireOp",EDGE,"E102.MirrorCS"),sQuery(id+"F0.wireOp",EDGE,"E103.MirrorC"),sQuery(id+"F0.wireOp",EDGE,"E104.MirrorC"),sQuery(id+"F0.wireOp",EDGE,"E107.MirrorCS"),sQuery(id+"F0.wireOp",EDGE,"E108.MirrorCS"),sQuery(id+"F0.wireOp",EDGE,"E109.MirrorCS"),sQuery(id+"F0.wireOp",EDGE,"E110.MirrorC"),sQuery(id+"F0.wireOp",EDGE,"E112.MirrorCS"),sQuery(id+"F0.wireOp",EDGE,"E120.MirrorCS"),sQuery(id+"F0.wireOp",EDGE,"E121.MirrorCS"),sQuery(id+"F0.wireOp",EDGE,"E122.MirrorCS"),sQuery(id+"F0.wireOp",EDGE,"E127.MirrorCS"),sQuery(id+"F0.wireOp",EDGE,"E131.MirrorCS"),sQuery(id+"F0.wireOp",EDGE,"E132.MirrorC"),sQuery(id+"F0.wireOp",EDGE,"E136.MirrorCS"),sQuery(id+"F0.wireOp",EDGE,"E137.MirrorCS"),sQuery(id+"F0.wireOp",EDGE,"E143.MirrorC"),sQuery(id+"F0.wireOp",EDGE,"E146.MirrorCS"),sQuery(id+"F0.wireOp",EDGE,"E147.MirrorCS"),sQuery(id+"F0.wireOp",EDGE,"E149.MirrorCS"),sQuery(id+"F0.wireOp",EDGE,"E150.MirrorCS"),sQuery(id+"F0.wireOp",EDGE,"E151.MirrorCS"),sQuery(id+"F0.wireOp",EDGE,"E152.MirrorCS"),sQuery(id+"F0.wireOp",EDGE,"E153.filletArc"),sQuery(id+"F0.wireOp",EDGE,"E154.filletArc"),sQuery(id+"F0.wireOp",EDGE,"E155.filletArc"),sQuery(id+"F0.wireOp",EDGE,"E156.filletArc"),sQuery(id+"F0.wireOp",EDGE,"E157"),sQuery(id+"F0.wireOp",EDGE,"E158"),sQuery(id+"F0.wireOp",EDGE,"E159"),sQuery(id+"F0.wireOp",EDGE,"E160"),sQuery(id+"F0.wireOp",EDGE,"E161.MirrorCS"),sQuery(id+"F0.wireOp",EDGE,"E162.filletArc"),sQuery(id+"F0.wireOp",EDGE,"E163.filletArc"),sQuery(id+"F0.wireOp",EDGE,"E164.filletArc"),sQuery(id+"F0.wireOp",EDGE,"E165.filletArc"),sQuery(id+"F0.wireOp",EDGE,"E166.filletArc"),sQuery(id+"F0.wireOp",EDGE,"E167.filletArc"),sQuery(id+"F0.wireOp",EDGE,"E168.MirrorCS"),sQuery(id+"F0.wireOp",EDGE,"E169.MirrorCS"),sQuery(id+"F0.wireOp",EDGE,"E170"),sQuery(id+"F0.wireOp",EDGE,"E171.MirrorCS"),sQuery(id+"F0.wireOp",EDGE,"E172.MirrorCS"),sQuery(id+"F0.wireOp",EDGE,"E173.MirrorCS"),sQuery(id+"F0.wireOp",EDGE,"cdnWEf1f-NTT4-Ris5-EAQB-sNyYZjwwmCeJ")])],"isStart":false});
            var sketch = newSketch(context, id + "F6", { "sketchPlane" : qUnion([Q0])});
            skCircle(sketch, "E241", {"center": v(-14, -23.5) * mm, "radius": 0.5 * mm});
            skCircle(sketch, "E242", {"center": v(-15.5, -23.5) * mm, "radius": 0.5 * mm});
            skCircle(sketch, "E243", {"center": v(-15.5, -26.5) * mm, "radius": 0.5 * mm});
            skCircle(sketch, "E244", {"center": v(-14, -26.5) * mm, "radius": 0.5 * mm});
            skCircle(sketch, "E245.MirrorC", {"center": v(14, -26.5) * mm, "radius": 0.5 * mm});
            skCircle(sketch, "E246.MirrorC", {"center": v(15.5, -23.5) * mm, "radius": 0.5 * mm});
            skCircle(sketch, "E247.MirrorC", {"center": v(15.5, -26.5) * mm, "radius": 0.5 * mm});
            skCircle(sketch, "E248.MirrorC", {"center": v(14, -23.5) * mm, "radius": 0.5 * mm});
            skSolve(sketch);
        }
        {
            var Q0;
            Q0 = qSketchRegion(id + "F6", true);
            extrude(context, id + "F7", {"entities" : qUnion([Q0]), "operationType" : NewBodyOperationType.REMOVE, "oppositeDirection" : true, "depth" : 25 * mm});
        }
    });
